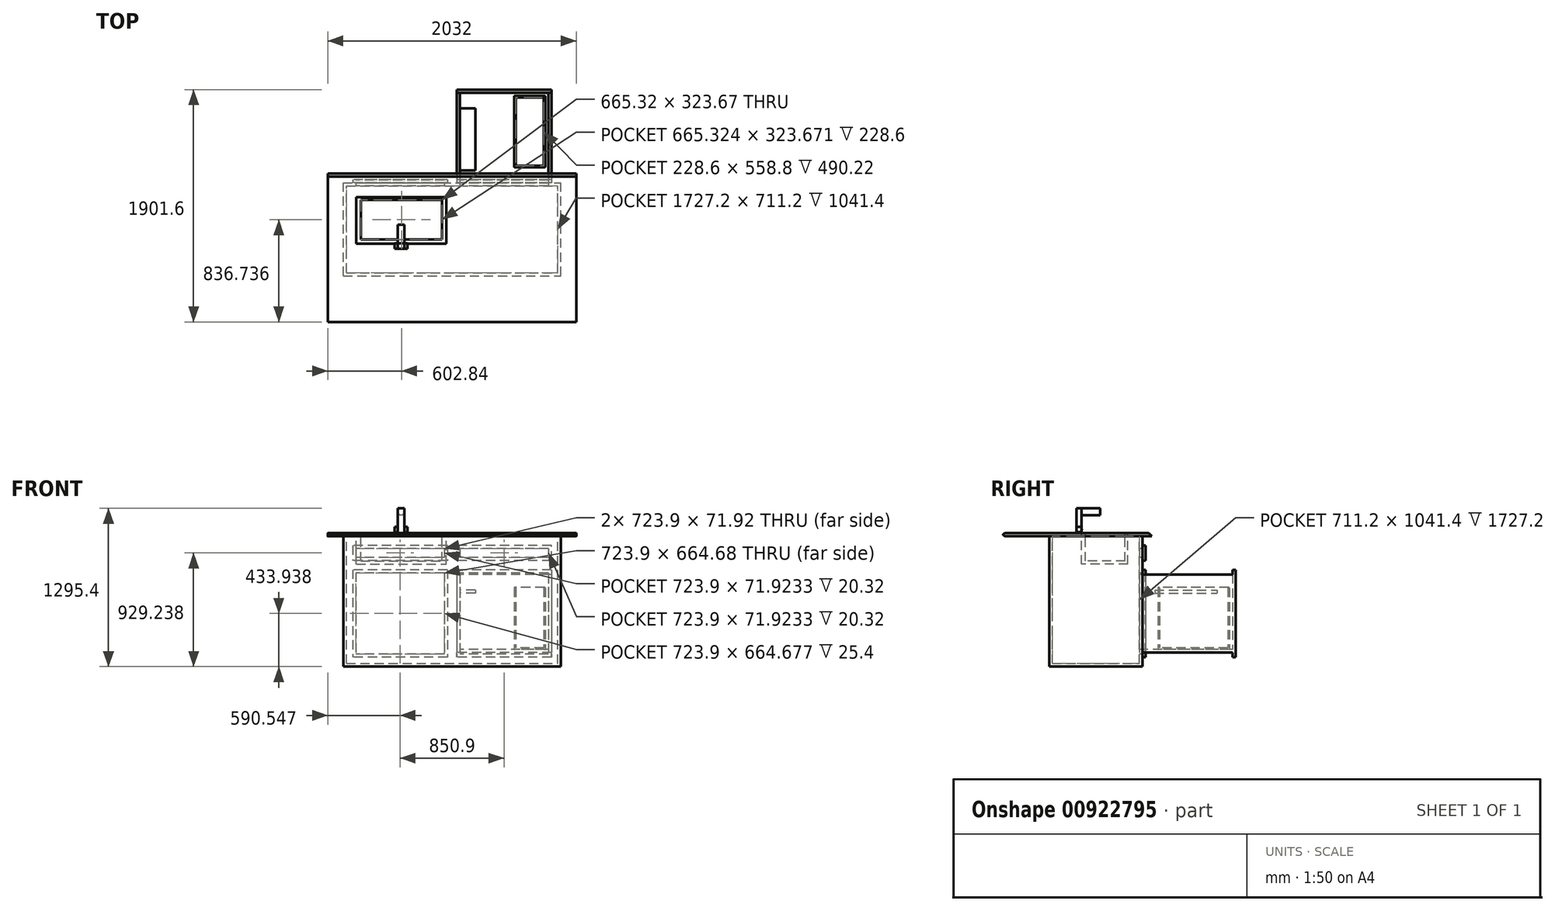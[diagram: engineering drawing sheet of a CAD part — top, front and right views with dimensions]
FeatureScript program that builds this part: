
annotation { "Feature Type Name" : "Feature", "Feature Type Description" : "" }
export const myFeature = defineFeature(function(context is Context, id is Id, definition is map)
    precondition{}
    {
        {
            var Q0;
            Q0=qCreatedBy(makeId("Top.planeOp"),FACE);
            var sketch = newSketch(context, id + "F0", { "sketchPlane" : qUnion([Q0])});
            skLineSegment(sketch, "E0.bottom", {"start": v(-835.25, 993.52) * mm, "end": v(1196.75, 993.52) * mm});
            skLineSegment(sketch, "E0.top", {"start": v(-835.25, -276.48) * mm, "end": v(1196.75, -276.48) * mm});
            skLineSegment(sketch, "E0.left", {"start": v(-835.25, 993.52) * mm, "end": v(-835.25, -276.48) * mm});
            skLineSegment(sketch, "E0.right", {"start": v(1196.75, 993.52) * mm, "end": v(1196.75, -276.48) * mm});
            skSolve(sketch);
        }
        {
            var Q0;
            Q0 = qSketchRegion(id + "F0", true);
            extrude(context, id + "F1", {"entities" : qUnion([Q0]), "depth" : 25.4 * mm, "offsetDistance" : 25.4 * mm});
        }
        {
            var Q0;
            Q0=makeQuery(id+"F1.opExtrude","CAP_FACE",FACE,{"disambiguationData":[OSD([sQuery(id+"F0.wireOp",EDGE,"E0.bottom"),sQuery(id+"F0.wireOp",EDGE,"E0.top"),sQuery(id+"F0.wireOp",EDGE,"E0.left"),sQuery(id+"F0.wireOp",EDGE,"E0.right")])],"isStart":true});
            var sketch = newSketch(context, id + "F2", { "sketchPlane" : qUnion([Q0])});
            skLineSegment(sketch, "E1.bottom", {"start": v(-708.25, -104.52) * mm, "end": v(1069.75, -104.52) * mm});
            skLineSegment(sketch, "E1.top", {"start": v(-708.25, -866.52) * mm, "end": v(1069.75, -866.52) * mm});
            skLineSegment(sketch, "E1.left", {"start": v(-708.25, -104.52) * mm, "end": v(-708.25, -866.52) * mm});
            skLineSegment(sketch, "E1.right", {"start": v(1069.75, -104.52) * mm, "end": v(1069.75, -866.52) * mm});
            skSolve(sketch);
        }
        {
            var Q0;
            Q0 = qSketchRegion(id + "F2", true);
            extrude(context, id + "F3", {"entities" : qUnion([Q0]), "operationType" : NewBodyOperationType.ADD, "depth" : 1066.8 * mm, "offsetDistance" : 25.4 * mm});
        }
        {
            var Q0;
            Q0=makeQuery(id+"F3.opExtrude","SWEPT_FACE",FACE,{"disambiguationData":[OSD([sQuery(id+"F2.wireOp",EDGE,"E1.top")])]});
            var sketch = newSketch(context, id + "F4", { "sketchPlane" : qUnion([Q0])});
            skLineSegment(sketch, "E2.bottom", {"start": v(-993.55, -198.92) * mm, "end": v(-218.85, -198.92) * mm});
            skLineSegment(sketch, "E2.top", {"start": v(-993.55, -76.2) * mm, "end": v(-218.85, -76.2) * mm});
            skLineSegment(sketch, "E2.left", {"start": v(-993.55, -198.92) * mm, "end": v(-993.55, -76.2) * mm});
            skLineSegment(sketch, "E2.right", {"start": v(-218.85, -198.92) * mm, "end": v(-218.85, -76.2) * mm});
            skLineSegment(sketch, "E3.bottom", {"start": v(-142.65, -76.2) * mm, "end": v(632.05, -76.2) * mm});
            skLineSegment(sketch, "E3.top", {"start": v(-142.65, -198.92) * mm, "end": v(632.05, -198.92) * mm});
            skLineSegment(sketch, "E3.left", {"start": v(-142.65, -76.2) * mm, "end": v(-142.65, -198.92) * mm});
            skLineSegment(sketch, "E3.right", {"start": v(632.05, -76.2) * mm, "end": v(632.05, -198.92) * mm});
            skSolve(sketch);
        }
        {
            var Q0;
            Q0 = qSketchRegion(id + "F4", true);
            extrude(context, id + "F5", {"entities" : qUnion([Q0]), "operationType" : NewBodyOperationType.ADD, "depth" : 25.4 * mm, "offsetDistance" : 25.4 * mm});
        }
        {
            var Q0;
            Q0=makeQuery(id+"F5.opExtrude","CAP_FACE",FACE,{"disambiguationData":[OSD([sQuery(id+"F4.wireOp",EDGE,"E2.bottom"),sQuery(id+"F4.wireOp",EDGE,"E2.top"),sQuery(id+"F4.wireOp",EDGE,"E2.left"),sQuery(id+"F4.wireOp",EDGE,"E2.right")])],"isStart":false});
            var sketch = newSketch(context, id + "F6", { "sketchPlane" : qUnion([Q0])});
            skLineSegment(sketch, "E4.bottom", {"start": v(-968.15, -101.6) * mm, "end": v(-244.25, -101.6) * mm});
            skLineSegment(sketch, "E4.top", {"start": v(-968.15, -173.52) * mm, "end": v(-244.25, -173.52) * mm});
            skLineSegment(sketch, "E4.left", {"start": v(-968.15, -101.6) * mm, "end": v(-968.15, -173.52) * mm});
            skLineSegment(sketch, "E4.right", {"start": v(-244.25, -101.6) * mm, "end": v(-244.25, -173.52) * mm});
            skLineSegment(sketch, "E5.bottom", {"start": v(-117.25, -101.6) * mm, "end": v(606.65, -101.6) * mm});
            skLineSegment(sketch, "E5.top", {"start": v(-117.25, -173.52) * mm, "end": v(606.65, -173.52) * mm});
            skLineSegment(sketch, "E5.left", {"start": v(-117.25, -101.6) * mm, "end": v(-117.25, -173.52) * mm});
            skLineSegment(sketch, "E5.right", {"start": v(606.65, -101.6) * mm, "end": v(606.65, -173.52) * mm});
            skSolve(sketch);
        }
        {
            var Q0;
            Q0 = qSketchRegion(id + "F6", true);
            extrude(context, id + "F7", {"entities" : qUnion([Q0]), "operationType" : NewBodyOperationType.REMOVE, "oppositeDirection" : true, "depth" : 5.08 * mm, "offsetDistance" : 25.4 * mm});
        }
        {
            var Q0;
            Q0=makeQuery(id+"F3.opExtrude","SWEPT_FACE",FACE,{"disambiguationData":[OSD([sQuery(id+"F2.wireOp",EDGE,"E1.top")])]});
            var sketch = newSketch(context, id + "F8", { "sketchPlane" : qUnion([Q0])});
            skLineSegment(sketch, "E6.bottom", {"start": v(-993.55, -275.12) * mm, "end": v(-218.85, -275.12) * mm});
            skLineSegment(sketch, "E6.top", {"start": v(-993.55, -990.6) * mm, "end": v(-218.85, -990.6) * mm});
            skLineSegment(sketch, "E6.left", {"start": v(-993.55, -275.12) * mm, "end": v(-993.55, -990.6) * mm});
            skLineSegment(sketch, "E6.right", {"start": v(-218.85, -275.12) * mm, "end": v(-218.85, -990.6) * mm});
            skLineSegment(sketch, "E7.bottom", {"start": v(-142.65, -275.12) * mm, "end": v(632.05, -275.12) * mm});
            skLineSegment(sketch, "E7.top", {"start": v(-142.65, -990.6) * mm, "end": v(632.05, -990.6) * mm});
            skLineSegment(sketch, "E7.left", {"start": v(-142.65, -275.12) * mm, "end": v(-142.65, -990.6) * mm});
            skLineSegment(sketch, "E7.right", {"start": v(632.05, -275.12) * mm, "end": v(632.05, -990.6) * mm});
            skSolve(sketch);
        }
        {
            var Q0;
            Q0=makeQuery(id+"F8.imprint","IMPRINT",FACE,{"disambiguationData":[TD([[makeQuery(id+"F8.imprint","IMPRINT",EDGE,{"derivedFrom":sQuery(id+"F8.wireOp",EDGE,"E7.bottom")}),-1.0]])]});
            extrude(context, id + "F9", {"entities" : qUnion([Q0]), "operationType" : NewBodyOperationType.ADD, "depth" : 25.4 * mm, "offsetDistance" : 25.4 * mm});
        }
        {
            var Q0;
            Q0=makeQuery(id+"F8.imprint","IMPRINT",FACE,{"disambiguationData":[TD([[makeQuery(id+"F8.imprint","IMPRINT",EDGE,{"derivedFrom":sQuery(id+"F8.wireOp",EDGE,"E6.bottom")}),-1.0]])]});
            var Q1;
            Q1=sQuery(id+"F8.wireOp",EDGE,"E7.bottom");
            extrude(context, id + "F10", {"entities" : qUnion([Q0]), "operationType" : NewBodyOperationType.ADD, "surfaceEntities" : qUnion([Q1]), "depth" : 762 * mm, "offsetDistance" : 25.4 * mm});
        }
        {
            var Q0;
            Q0=makeQuery(id+"F10.opExtrude","SWEPT_FACE",FACE,{"disambiguationData":[OSD([sQuery(id+"F8.wireOp",EDGE,"E6.right")])]});
            var sketch = newSketch(context, id + "F11", { "sketchPlane" : qUnion([Q0])});
            skLineSegment(sketch, "E8.bottom", {"start": v(-1603.12, -275.12) * mm, "end": v(-866.52, -275.12) * mm});
            skLineSegment(sketch, "E8.top", {"start": v(-1603.12, -313.22) * mm, "end": v(-866.52, -313.22) * mm});
            skLineSegment(sketch, "E8.left", {"start": v(-1603.12, -275.12) * mm, "end": v(-1603.12, -313.22) * mm});
            skLineSegment(sketch, "E8.right", {"start": v(-866.52, -275.12) * mm, "end": v(-866.52, -313.22) * mm});
            skLineSegment(sketch, "E9.bottom", {"start": v(-1603.12, -990.6) * mm, "end": v(-866.52, -990.6) * mm});
            skLineSegment(sketch, "E9.top", {"start": v(-1603.12, -952.5) * mm, "end": v(-866.52, -952.5) * mm});
            skLineSegment(sketch, "E9.left", {"start": v(-1603.12, -990.6) * mm, "end": v(-1603.12, -952.5) * mm});
            skLineSegment(sketch, "E9.right", {"start": v(-866.52, -990.6) * mm, "end": v(-866.52, -952.5) * mm});
            skSolve(sketch);
        }
        {
            var Q0;
            Q0 = qSketchRegion(id + "F11", true);
            extrude(context, id + "F12", {"entities" : qUnion([Q0]), "operationType" : NewBodyOperationType.REMOVE, "oppositeDirection" : true, "depth" : 787.4 * mm, "offsetDistance" : 25.4 * mm});
        }
        {
            var Q0;
            Q0=makeQuery(id+"F12.boolean.opBoolean","COPY",FACE,{"derivedFrom":makeQuery(id+"F12.opExtrude","SWEPT_FACE",FACE,{"disambiguationData":[OSD([sQuery(id+"F11.wireOp",EDGE,"E8.top")])]})});
            shell(context, id + "F13", {"entities" : qUnion([Q0]), "thickness" : 25.4 * mm});
        }
        {
            var Q0;
            Q0=makeQuery(id+"F9.opExtrude","CAP_FACE",FACE,{"disambiguationData":[OSD([sQuery(id+"F8.wireOp",EDGE,"E7.bottom"),sQuery(id+"F8.wireOp",EDGE,"E7.top"),sQuery(id+"F8.wireOp",EDGE,"E7.left"),sQuery(id+"F8.wireOp",EDGE,"E7.right")])],"isStart":false});
            var sketch = newSketch(context, id + "F14", { "sketchPlane" : qUnion([Q0])});
            skLineSegment(sketch, "E10.bottom", {"start": v(-117.25, -300.52) * mm, "end": v(606.65, -300.52) * mm});
            skLineSegment(sketch, "E10.top", {"start": v(-117.25, -965.2) * mm, "end": v(606.65, -965.2) * mm});
            skLineSegment(sketch, "E10.left", {"start": v(-117.25, -300.52) * mm, "end": v(-117.25, -965.2) * mm});
            skLineSegment(sketch, "E10.right", {"start": v(606.65, -300.52) * mm, "end": v(606.65, -965.2) * mm});
            skSolve(sketch);
        }
        {
            var Q0;
            Q0 = qSketchRegion(id + "F14", true);
            extrude(context, id + "F15", {"entities" : qUnion([Q0]), "operationType" : NewBodyOperationType.REMOVE, "oppositeDirection" : true, "depth" : 5.08 * mm, "offsetDistance" : 25.4 * mm});
        }
        {
            var Q0;
            Q0=makeQuery(id+"F10.opExtrude","CAP_FACE",FACE,{"disambiguationData":[OSD([sQuery(id+"F8.wireOp",EDGE,"E6.bottom"),sQuery(id+"F8.wireOp",EDGE,"E6.top"),sQuery(id+"F8.wireOp",EDGE,"E6.left"),sQuery(id+"F8.wireOp",EDGE,"E6.right")])],"isStart":false});
            var sketch = newSketch(context, id + "F16", { "sketchPlane" : qUnion([Q0])});
            skLineSegment(sketch, "E11.bottom", {"start": v(-968.15, -300.52) * mm, "end": v(-244.25, -300.52) * mm});
            skLineSegment(sketch, "E11.top", {"start": v(-968.15, -965.2) * mm, "end": v(-244.25, -965.2) * mm});
            skLineSegment(sketch, "E11.left", {"start": v(-968.15, -300.52) * mm, "end": v(-968.15, -965.2) * mm});
            skLineSegment(sketch, "E11.right", {"start": v(-244.25, -300.52) * mm, "end": v(-244.25, -965.2) * mm});
            skSolve(sketch);
        }
        {
            var Q0;
            Q0 = qSketchRegion(id + "F16", true);
            extrude(context, id + "F17", {"entities" : qUnion([Q0]), "operationType" : NewBodyOperationType.REMOVE, "oppositeDirection" : true, "depth" : 5.08 * mm, "offsetDistance" : 25.4 * mm});
        }
        {
            var Q0;
            Q0=makeQuery(id+"F1.opExtrude","CAP_EDGE",EDGE,{"disambiguationData":[OSD([sQuery(id+"F0.wireOp",EDGE,"E0.top")])],"isStart":false});
            var Q1;
            Q1=makeQuery(id+"F1.opExtrude","CAP_EDGE",EDGE,{"disambiguationData":[OSD([sQuery(id+"F0.wireOp",EDGE,"E0.top")])],"isStart":true});
            fillet(context, id + "F18", {"entities" : qUnion([Q0, Q1]), "radius" : 25.4 * mm, "tangentPropagation" : true, "allowEdgeOverflow" : false});
        }
        {
            var Q0;
            Q0=makeQuery(id+"F1.opExtrude","CAP_EDGE",EDGE,{"disambiguationData":[OSD([sQuery(id+"F0.wireOp",EDGE,"E0.bottom")])],"isStart":false});
            chamfer(context, id + "F19", {"entities" : qUnion([Q0]), "width" : 76.2 * mm, "tangentPropagation" : true});
        }
        {
            var Q0;
            Q0=makeQuery(id+"F13.opShell","OFFSET_FACE",FACE,{"disambiguationData":[OSD([sQuery(id+"F8.wireOp",EDGE,"E6.right")])]});
            var sketch = newSketch(context, id + "F20", { "sketchPlane" : qUnion([Q0])});
            skLineSegment(sketch, "E12.bottom", {"start": v(968.12, -440.22) * mm, "end": v(1476.12, -440.22) * mm});
            skLineSegment(sketch, "E12.top", {"start": v(968.12, -465.62) * mm, "end": v(1476.12, -465.62) * mm});
            skLineSegment(sketch, "E12.left", {"start": v(968.12, -440.22) * mm, "end": v(968.12, -465.62) * mm});
            skLineSegment(sketch, "E12.right", {"start": v(1476.12, -440.22) * mm, "end": v(1476.12, -465.62) * mm});
            skSolve(sketch);
        }
        {
            var Q0;
            Q0 = qSketchRegion(id + "F20", true);
            extrude(context, id + "F21", {"entities" : qUnion([Q0]), "operationType" : NewBodyOperationType.ADD, "depth" : 127 * mm, "offsetDistance" : 25.4 * mm});
        }
        {
            var Q0;
            Q0=makeQuery(id+"F13.opShell","OFFSET_FACE",FACE,{"disambiguationData":[OSD([sQuery(id+"F11.wireOp",EDGE,"E9.top")])]});
            cPlane(context, id + "F22", {"entities" : qUnion([Q0]), "cplaneType" : CPlaneType.OFFSET, "offset" : 0 * mm, "width" : 152.4 * mm, "height" : 152.4 * mm});
        }
        {
            var Q0;
            Q0=qCreatedBy(id+"F22.planeOp",FACE);
            var sketch = newSketch(context, id + "F23", { "sketchPlane" : qUnion([Q0])});
            skLineSegment(sketch, "E13.bottom", {"start": v(942.75, 1577.72) * mm, "end": v(688.75, 1577.72) * mm});
            skLineSegment(sketch, "E13.top", {"start": v(942.75, 993.52) * mm, "end": v(688.75, 993.52) * mm});
            skLineSegment(sketch, "E13.left", {"start": v(942.75, 1577.72) * mm, "end": v(942.75, 993.52) * mm});
            skLineSegment(sketch, "E13.right", {"start": v(688.75, 1577.72) * mm, "end": v(688.75, 993.52) * mm});
            skSolve(sketch);
        }
        {
            var Q0;
            Q0 = qSketchRegion(id + "F23", true);
            extrude(context, id + "F24", {"entities" : qUnion([Q0]), "depth" : 508 * mm, "offsetDistance" : 25.4 * mm});
        }
        {
            var Q0;
            Q0=makeQuery(id+"F24.opExtrude","CAP_FACE",FACE,{"disambiguationData":[OSD([sQuery(id+"F23.wireOp",EDGE,"E13.bottom"),sQuery(id+"F23.wireOp",EDGE,"E13.top"),sQuery(id+"F23.wireOp",EDGE,"E13.left"),sQuery(id+"F23.wireOp",EDGE,"E13.right")])],"isStart":false});
            shell(context, id + "F25", {"entities" : qUnion([Q0]), "thickness" : 12.7 * mm});
        }
        {
            var Q0;
            Q0=makeQuery(id+"F24.opExtrude","SWEPT_EDGE",EDGE,{"disambiguationData":[OSD([sQuery(id+"F23.wireOp",EDGE,"E13.bottom"),sQuery(id+"F23.wireOp",EDGE,"E13.right")])]});
            var Q1;
            Q1=makeQuery(id+"F24.opExtrude","SWEPT_EDGE",EDGE,{"disambiguationData":[OSD([sQuery(id+"F23.wireOp",EDGE,"E13.bottom"),sQuery(id+"F23.wireOp",EDGE,"E13.left")])]});
            var Q2;
            Q2=makeQuery(id+"F24.opExtrude","SWEPT_EDGE",EDGE,{"disambiguationData":[OSD([sQuery(id+"F23.wireOp",EDGE,"E13.top"),sQuery(id+"F23.wireOp",EDGE,"E13.right")])]});
            var Q3;
            Q3=makeQuery(id+"F24.opExtrude","SWEPT_EDGE",EDGE,{"disambiguationData":[OSD([sQuery(id+"F23.wireOp",EDGE,"E13.top"),sQuery(id+"F23.wireOp",EDGE,"E13.left")])]});
            var Q4;
            Q4=makeQuery(id+"F24.opExtrude","CAP_EDGE",EDGE,{"disambiguationData":[OSD([sQuery(id+"F23.wireOp",EDGE,"E13.left")])],"isStart":false});
            var Q5;
            {var subQ0=sQuery(id+"F23.wireOp",EDGE,"E13.left");Q5=makeQuery(id+"F25.opShell","OFFSET_EDGE",EDGE,{"disambiguationData":[OSD([subQ0]),TDD([makeQuery(id+"F24.opExtrude","CAP_EDGE",EDGE,{"disambiguationData":[OSD([subQ0])],"isStart":false})])]});}
            var Q6;
            Q6=makeQuery(id+"F24.opExtrude","CAP_EDGE",EDGE,{"disambiguationData":[OSD([sQuery(id+"F23.wireOp",EDGE,"E13.bottom")])],"isStart":false});
            var Q7;
            {var subQ0=sQuery(id+"F23.wireOp",EDGE,"E13.bottom");Q7=makeQuery(id+"F25.opShell","OFFSET_EDGE",EDGE,{"disambiguationData":[OSD([subQ0]),TDD([makeQuery(id+"F24.opExtrude","CAP_EDGE",EDGE,{"disambiguationData":[OSD([subQ0])],"isStart":false})])]});}
            var Q8;
            {var subQ0=sQuery(id+"F23.wireOp",EDGE,"E13.right");Q8=makeQuery(id+"F25.opShell","OFFSET_EDGE",EDGE,{"disambiguationData":[OSD([subQ0]),TDD([makeQuery(id+"F24.opExtrude","CAP_EDGE",EDGE,{"disambiguationData":[OSD([subQ0])],"isStart":false})])]});}
            var Q9;
            Q9=makeQuery(id+"F24.opExtrude","CAP_EDGE",EDGE,{"disambiguationData":[OSD([sQuery(id+"F23.wireOp",EDGE,"E13.right")])],"isStart":false});
            var Q10;
            {var subQ0=sQuery(id+"F23.wireOp",EDGE,"E13.top");Q10=makeQuery(id+"F25.opShell","OFFSET_EDGE",EDGE,{"disambiguationData":[OSD([subQ0]),TDD([makeQuery(id+"F24.opExtrude","CAP_EDGE",EDGE,{"disambiguationData":[OSD([subQ0])],"isStart":false})])]});}
            var Q11;
            Q11=makeQuery(id+"F24.opExtrude","CAP_EDGE",EDGE,{"disambiguationData":[OSD([sQuery(id+"F23.wireOp",EDGE,"E13.top")])],"isStart":false});
            fillet(context, id + "F26", {"entities" : qUnion([Q0, Q1, Q2, Q3, Q4, Q5, Q6, Q7, Q8, Q9, Q10, Q11]), "radius" : 5.08 * mm, "tangentPropagation" : true, "allowEdgeOverflow" : false});
        }
        {
            var Q0;
            Q0=makeQuery(id+"F1.opExtrude","CAP_FACE",FACE,{"disambiguationData":[OSD([sQuery(id+"F0.wireOp",EDGE,"E0.bottom"),sQuery(id+"F0.wireOp",EDGE,"E0.top"),sQuery(id+"F0.wireOp",EDGE,"E0.left"),sQuery(id+"F0.wireOp",EDGE,"E0.right")])],"isStart":false});
            var sketch = newSketch(context, id + "F27", { "sketchPlane" : qUnion([Q0])});
            skLineSegment(sketch, "E14.bottom", {"start": v(-601.81, 747.53) * mm, "end": v(133.95, 747.53) * mm});
            skLineSegment(sketch, "E14.top", {"start": v(-601.81, 367.47) * mm, "end": v(133.95, 367.47) * mm});
            skLineSegment(sketch, "E14.left", {"start": v(-601.81, 747.53) * mm, "end": v(-601.81, 367.47) * mm});
            skLineSegment(sketch, "E14.right", {"start": v(133.95, 747.53) * mm, "end": v(133.95, 367.47) * mm});
            skSolve(sketch);
        }
        {
            var Q0;
            Q0=makeQuery(id+"F27.imprint","IMPRINT",FACE,{"disambiguationData":[TD([[makeQuery(id+"F27.imprint","IMPRINT",EDGE,{"derivedFrom":sQuery(id+"F27.wireOp",EDGE,"E14.bottom")}),-1.0]])]});
            extrude(context, id + "F28", {"entities" : qUnion([Q0]), "oppositeDirection" : true, "depth" : 254 * mm, "offsetDistance" : 25.4 * mm});
        }
        {
            var Q0;
            Q0=makeQuery(id+"F28.opExtrude","CAP_FACE",FACE,{"disambiguationData":[OSD([sQuery(id+"F27.wireOp",EDGE,"E14.bottom"),sQuery(id+"F27.wireOp",EDGE,"E14.top"),sQuery(id+"F27.wireOp",EDGE,"E14.left"),sQuery(id+"F27.wireOp",EDGE,"E14.right")])],"isStart":true});
            var sketch = newSketch(context, id + "F29", { "sketchPlane" : qUnion([Q0])});
            skLineSegment(sketch, "E15.bottom", {"start": v(-565.07, 725.5) * mm, "end": v(100.25, 725.5) * mm});
            skLineSegment(sketch, "E15.top", {"start": v(-565.07, 401.82) * mm, "end": v(100.25, 401.82) * mm});
            skLineSegment(sketch, "E15.left", {"start": v(-565.07, 725.5) * mm, "end": v(-565.07, 401.82) * mm});
            skLineSegment(sketch, "E15.right", {"start": v(100.25, 725.5) * mm, "end": v(100.25, 401.82) * mm});
            skPoint(sketch, "E15.middle", {"position": v(-232.41, 563.66) * mm});
            skSolve(sketch);
        }
        {
            var Q0;
            Q0=makeQuery(id+"F29.imprint","IMPRINT",FACE,{"disambiguationData":[TD([[makeQuery(id+"F29.imprint","IMPRINT",EDGE,{"derivedFrom":sQuery(id+"F29.wireOp",EDGE,"E15.bottom")}),-1.0]])]});
            extrude(context, id + "F30", {"entities" : qUnion([Q0]), "operationType" : NewBodyOperationType.REMOVE, "oppositeDirection" : true, "depth" : 228.6 * mm, "offsetDistance" : 25.4 * mm});
        }
        {
            var Q0;
            Q0=makeQuery(id+"F1.opExtrude","CAP_FACE",FACE,{"disambiguationData":[OSD([sQuery(id+"F0.wireOp",EDGE,"E0.bottom"),sQuery(id+"F0.wireOp",EDGE,"E0.top"),sQuery(id+"F0.wireOp",EDGE,"E0.left"),sQuery(id+"F0.wireOp",EDGE,"E0.right")])],"isStart":false});
            var sketch = newSketch(context, id + "F31", { "sketchPlane" : qUnion([Q0])});
            skLineSegment(sketch, "E16.bottom", {"start": v(-261.9, 369.91) * mm, "end": v(-207.42, 369.91) * mm});
            skLineSegment(sketch, "E16.top", {"start": v(-261.9, 326.33) * mm, "end": v(-207.42, 326.33) * mm});
            skLineSegment(sketch, "E16.left", {"start": v(-261.9, 369.91) * mm, "end": v(-261.9, 326.33) * mm});
            skLineSegment(sketch, "E16.right", {"start": v(-207.42, 369.91) * mm, "end": v(-207.42, 326.33) * mm});
            skSolve(sketch);
        }
        {
            var Q0;
            Q0 = qSketchRegion(id + "F31", true);
            extrude(context, id + "F32", {"entities" : qUnion([Q0]), "depth" : 203.2 * mm, "offsetDistance" : 25.4 * mm});
        }
        {
            var Q0;
            Q0=makeQuery(id+"F32.opExtrude","SWEPT_FACE",FACE,{"disambiguationData":[OSD([sQuery(id+"F31.wireOp",EDGE,"E16.bottom")])]});
            var sketch = newSketch(context, id + "F33", { "sketchPlane" : qUnion([Q0])});
            skCircle(sketch, "E17", {"center": v(234.66, 200.68) * mm, "radius": 27.24 * mm});
            skPoint(sketch, "E17.centerSnap0", {"position": v(234.66, 228.6) * mm});
            skSolve(sketch);
        }
        {
            var Q0;
            Q0 = qSketchRegion(id + "F33", true);
            extrude(context, id + "F34", {"entities" : qUnion([Q0]), "operationType" : NewBodyOperationType.ADD, "depth" : 152.4 * mm, "offsetDistance" : 25.4 * mm});
        }
        {
            var Q0;
            Q0=makeQuery(id+"F32.opExtrude","SWEPT_FACE",FACE,{"disambiguationData":[OSD([sQuery(id+"F31.wireOp",EDGE,"E16.left")])]});
            var sketch = newSketch(context, id + "F35", { "sketchPlane" : qUnion([Q0])});
            skCircle(sketch, "E18", {"center": v(-348.35, 54.08) * mm, "radius": 22.02 * mm});
            skSolve(sketch);
        }
        {
            var Q0;
            Q0 = qSketchRegion(id + "F35", true);
            extrude(context, id + "F36", {"entities" : qUnion([Q0]), "depth" : 25.4 * mm, "offsetDistance" : 25.4 * mm});
        }
        {
            var Q0;
            Q0=makeQuery(id+"F32.opExtrude","SWEPT_FACE",FACE,{"disambiguationData":[OSD([sQuery(id+"F31.wireOp",EDGE,"E16.right")])]});
            var sketch = newSketch(context, id + "F37", { "sketchPlane" : qUnion([Q0])});
            skCircle(sketch, "E19", {"center": v(347.9, 55.47) * mm, "radius": 22.02 * mm});
            skSolve(sketch);
        }
        {
            var Q0;
            Q0 = qSketchRegion(id + "F37", true);
            extrude(context, id + "F38", {"entities" : qUnion([Q0]), "depth" : 25.4 * mm, "offsetDistance" : 25.4 * mm});
        }
    });
